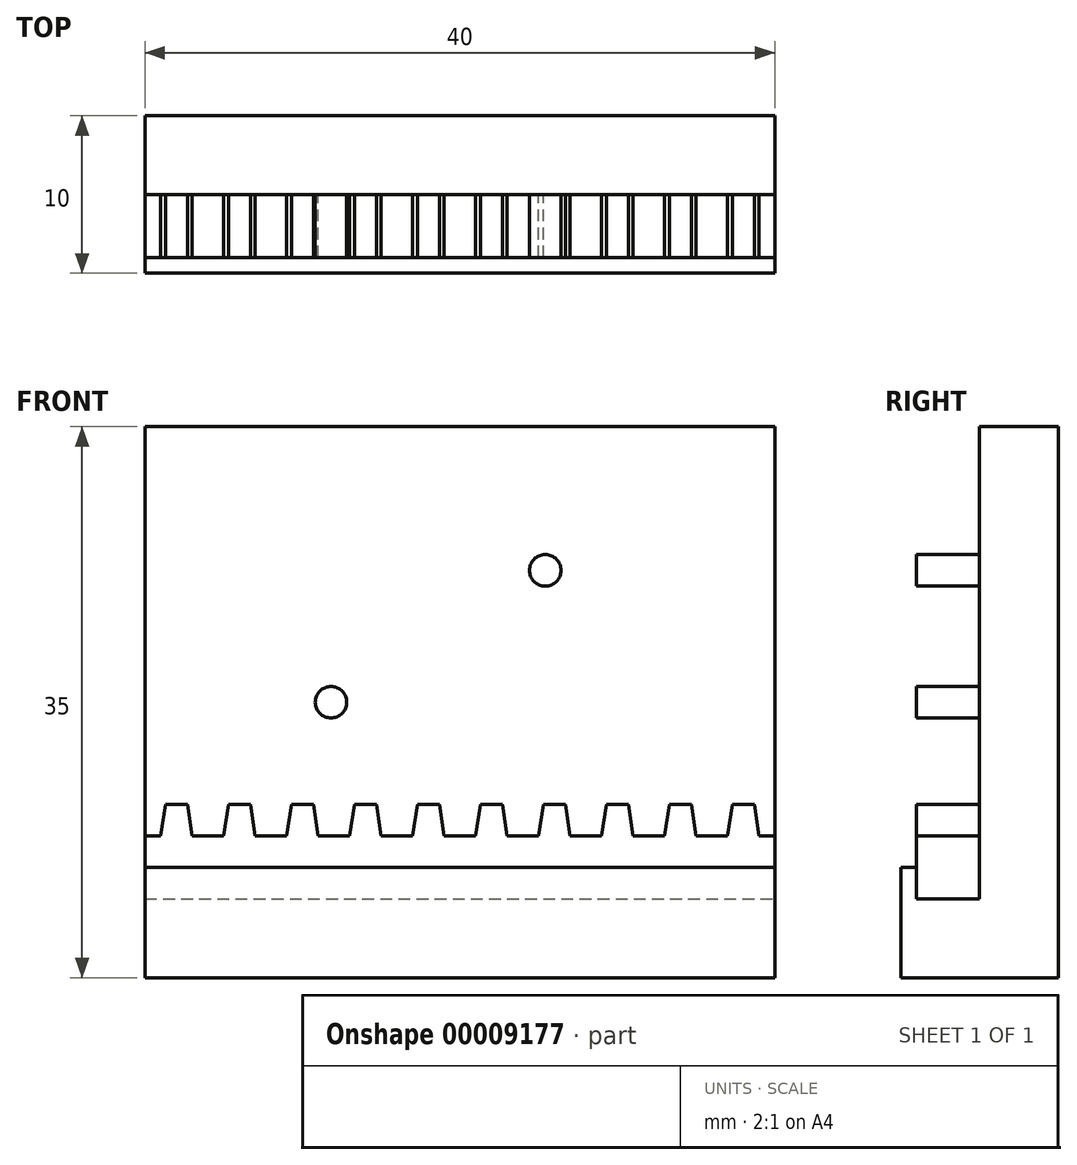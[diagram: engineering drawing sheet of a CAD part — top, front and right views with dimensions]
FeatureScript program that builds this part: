
annotation { "Feature Type Name" : "Feature", "Feature Type Description" : "" }
export const myFeature = defineFeature(function(context is Context, id is Id, definition is map)
    precondition{}
    {
        {
            var Q0;
            Q0=qCreatedBy(makeId("Front.planeOp"),FACE);
            var sketch = newSketch(context, id + "F0", { "sketchPlane" : qUnion([Q0])});
            skLineSegment(sketch, "E0.rect.bottom", {"start": v(-20, 17.5) * mm, "end": v(20, 17.5) * mm});
            skLineSegment(sketch, "E0.rect.top", {"start": v(-20, -17.5) * mm, "end": v(20, -17.5) * mm});
            skLineSegment(sketch, "E0.rect.left", {"start": v(-20, 17.5) * mm, "end": v(-20, -17.5) * mm});
            skLineSegment(sketch, "E0.rect.right", {"start": v(20, 17.5) * mm, "end": v(20, -17.5) * mm});
            skPoint(sketch, "E0.rect.middle", {"position": v(0, 0) * mm});
            skSolve(sketch);
        }
        {
            var Q0;
            Q0 = qSketchRegion(id + "F0", true);
            extrude(context, id + "F1", {"entities" : qUnion([Q0]), "depth" : 10 * mm});
        }
        {
            var Q0;
            Q0=makeQuery(id+"F1.opExtrude","CAP_FACE",FACE,{"disambiguationData":[OSD([sQuery(id+"F0.wireOp",EDGE,"E0.rect.bottom"),sQuery(id+"F0.wireOp",EDGE,"E0.rect.top"),sQuery(id+"F0.wireOp",EDGE,"E0.rect.left"),sQuery(id+"F0.wireOp",EDGE,"E0.rect.right")])],"isStart":false});
            var sketch = newSketch(context, id + "F2", { "sketchPlane" : qUnion([Q0])});
            skLineSegment(sketch, "E1.bottom", {"start": v(-20, 17.5) * mm, "end": v(20, 17.5) * mm});
            skLineSegment(sketch, "E1.top", {"start": v(-20, -12.5) * mm, "end": v(20, -12.5) * mm});
            skLineSegment(sketch, "E1.left", {"start": v(-20, 17.5) * mm, "end": v(-20, -12.5) * mm});
            skLineSegment(sketch, "E1.right", {"start": v(20, 17.5) * mm, "end": v(20, -12.5) * mm});
            skSolve(sketch);
        }
        {
            var Q0;
            Q0=makeQuery(id+"F2.imprint","IMPRINT",FACE,{"disambiguationData":[TD([[makeQuery(id+"F2.imprint","IMPRINT",EDGE,{"derivedFrom":sQuery(id+"F2.wireOp",EDGE,"E1.bottom")}),-1.0]])]});
            extrude(context, id + "F3", {"entities" : qUnion([Q0]), "operationType" : NewBodyOperationType.REMOVE, "oppositeDirection" : true, "depth" : 5 * mm});
        }
        {
            var Q0;
            Q0=makeQuery(id+"F1.opExtrude","SWEPT_FACE",FACE,{"disambiguationData":[OSD([sQuery(id+"F0.wireOp",EDGE,"E0.rect.right")])]});
            var sketch = newSketch(context, id + "F4", { "sketchPlane" : qUnion([Q0])});
            skLineSegment(sketch, "E2.bottom", {"start": v(-10, -12.5) * mm, "end": v(-9, -12.5) * mm});
            skLineSegment(sketch, "E2.top", {"start": v(-10, -10.5) * mm, "end": v(-9, -10.5) * mm});
            skLineSegment(sketch, "E2.left", {"start": v(-10, -12.5) * mm, "end": v(-10, -10.5) * mm});
            skLineSegment(sketch, "E2.right", {"start": v(-9, -12.5) * mm, "end": v(-9, -10.5) * mm});
            skSolve(sketch);
        }
        {
            var Q0;
            Q0 = qSketchRegion(id + "F4", true);
            var Q1;
            Q1=makeQuery(id+"F1.opExtrude","SWEPT_FACE",FACE,{"disambiguationData":[OSD([sQuery(id+"F0.wireOp",EDGE,"E0.rect.left")])]});
            extrude(context, id + "F5", {"entities" : qUnion([Q0]), "operationType" : NewBodyOperationType.ADD, "endBound" : BoundingType.UP_TO_SURFACE, "oppositeDirection" : true, "endBoundEntityFace" : qUnion([Q1]), "depth" : 25 * mm});
        }
        {
            var Q0;
            Q0=makeQuery(id+"F3.boolean.opBoolean","COPY",FACE,{"derivedFrom":makeQuery(id+"F3.opExtrude","CAP_FACE",FACE,{"disambiguationData":[OSD([sQuery(id+"F2.wireOp",EDGE,"E1.bottom"),sQuery(id+"F2.wireOp",EDGE,"E1.top"),sQuery(id+"F2.wireOp",EDGE,"E1.left"),sQuery(id+"F2.wireOp",EDGE,"E1.right")])],"isStart":false})});
            var sketch = newSketch(context, id + "F6", { "sketchPlane" : qUnion([Q0])});
            skCircle(sketch, "E3", {"center": v(-8.18, 0) * mm, "radius": 1 * mm});
            skCircle(sketch, "E4", {"center": v(5.42, 8.37) * mm, "radius": 1 * mm});
            skSolve(sketch);
        }
        {
            var Q0;
            Q0 = qSketchRegion(id + "F6", true);
            extrude(context, id + "F7", {"entities" : qUnion([Q0]), "operationType" : NewBodyOperationType.ADD, "depth" : 4 * mm});
        }
        {
            var Q0;
            Q0=makeQuery(id+"F3.boolean.opBoolean","COPY",FACE,{"derivedFrom":makeQuery(id+"F3.opExtrude","CAP_FACE",FACE,{"disambiguationData":[OSD([sQuery(id+"F2.wireOp",EDGE,"E1.bottom"),sQuery(id+"F2.wireOp",EDGE,"E1.top"),sQuery(id+"F2.wireOp",EDGE,"E1.left"),sQuery(id+"F2.wireOp",EDGE,"E1.right")])],"isStart":false})});
            var sketch = newSketch(context, id + "F8", { "sketchPlane" : qUnion([Q0])});
            skLineSegment(sketch, "E5.bottom", {"start": v(-20, -12.5) * mm, "end": v(20, -12.5) * mm});
            skLineSegment(sketch, "E5.top", {"start": v(-20, -8.5) * mm, "end": v(20, -8.5) * mm});
            skLineSegment(sketch, "E5.left", {"start": v(-20, -12.5) * mm, "end": v(-20, -8.5) * mm});
            skLineSegment(sketch, "E5.right", {"start": v(20, -12.5) * mm, "end": v(20, -8.5) * mm});
            skLineSegment(sketch, "E6", {"start": v(-18, -8.5) * mm, "end": v(-18, -12.5) * mm, "construction": true});
            skLineSegment(sketch, "E7", {"start": v(-19, -8.5) * mm, "end": v(-18.7, -6.5) * mm});
            skLineSegment(sketch, "E8", {"start": v(-18.7, -6.5) * mm, "end": v(-18, -6.5) * mm});
            skLineSegment(sketch, "E9.MirrorCS", {"start": v(-17, -8.5) * mm, "end": v(-17.3, -6.5) * mm});
            skLineSegment(sketch, "E10.MirrorCS", {"start": v(-17.3, -6.5) * mm, "end": v(-18, -6.5) * mm});
            skLineSegment(sketch, "E11.1.0.0", {"start": v(-15, -8.5) * mm, "end": v(-14.7, -6.5) * mm});
            skLineSegment(sketch, "E11.1.0.1", {"start": v(-14.7, -6.5) * mm, "end": v(-14, -6.5) * mm});
            skLineSegment(sketch, "E11.1.0.2", {"start": v(-13.3, -6.5) * mm, "end": v(-14, -6.5) * mm});
            skLineSegment(sketch, "E11.1.0.3", {"start": v(-13, -8.5) * mm, "end": v(-13.3, -6.5) * mm});
            skLineSegment(sketch, "E11.2.0.0", {"start": v(-11, -8.5) * mm, "end": v(-10.7, -6.5) * mm});
            skLineSegment(sketch, "E11.2.0.1", {"start": v(-10.7, -6.5) * mm, "end": v(-10, -6.5) * mm});
            skLineSegment(sketch, "E11.2.0.2", {"start": v(-9.3, -6.5) * mm, "end": v(-10, -6.5) * mm});
            skLineSegment(sketch, "E11.2.0.3", {"start": v(-9, -8.5) * mm, "end": v(-9.3, -6.5) * mm});
            skLineSegment(sketch, "E11.3.0.0", {"start": v(-7, -8.5) * mm, "end": v(-6.7, -6.5) * mm});
            skLineSegment(sketch, "E11.3.0.1", {"start": v(-6.7, -6.5) * mm, "end": v(-6, -6.5) * mm});
            skLineSegment(sketch, "E11.3.0.2", {"start": v(-5.3, -6.5) * mm, "end": v(-6, -6.5) * mm});
            skLineSegment(sketch, "E11.3.0.3", {"start": v(-5, -8.5) * mm, "end": v(-5.3, -6.5) * mm});
            skLineSegment(sketch, "E11.4.0.0", {"start": v(-3, -8.5) * mm, "end": v(-2.7, -6.5) * mm});
            skLineSegment(sketch, "E11.4.0.1", {"start": v(-2.7, -6.5) * mm, "end": v(-2, -6.5) * mm});
            skLineSegment(sketch, "E11.4.0.2", {"start": v(-1.3, -6.5) * mm, "end": v(-2, -6.5) * mm});
            skLineSegment(sketch, "E11.4.0.3", {"start": v(-1, -8.5) * mm, "end": v(-1.3, -6.5) * mm});
            skLineSegment(sketch, "E11.5.0.0", {"start": v(1, -8.5) * mm, "end": v(1.3, -6.5) * mm});
            skLineSegment(sketch, "E11.5.0.1", {"start": v(1.3, -6.5) * mm, "end": v(2, -6.5) * mm});
            skLineSegment(sketch, "E11.5.0.2", {"start": v(2.7, -6.5) * mm, "end": v(2, -6.5) * mm});
            skLineSegment(sketch, "E11.5.0.3", {"start": v(3, -8.5) * mm, "end": v(2.7, -6.5) * mm});
            skLineSegment(sketch, "E11.6.0.0", {"start": v(5, -8.5) * mm, "end": v(5.3, -6.5) * mm});
            skLineSegment(sketch, "E11.6.0.1", {"start": v(5.3, -6.5) * mm, "end": v(6, -6.5) * mm});
            skLineSegment(sketch, "E11.6.0.2", {"start": v(6.7, -6.5) * mm, "end": v(6, -6.5) * mm});
            skLineSegment(sketch, "E11.6.0.3", {"start": v(7, -8.5) * mm, "end": v(6.7, -6.5) * mm});
            skLineSegment(sketch, "E11.7.0.0", {"start": v(9, -8.5) * mm, "end": v(9.3, -6.5) * mm});
            skLineSegment(sketch, "E11.7.0.1", {"start": v(9.3, -6.5) * mm, "end": v(10, -6.5) * mm});
            skLineSegment(sketch, "E11.7.0.2", {"start": v(10.7, -6.5) * mm, "end": v(10, -6.5) * mm});
            skLineSegment(sketch, "E11.7.0.3", {"start": v(11, -8.5) * mm, "end": v(10.7, -6.5) * mm});
            skLineSegment(sketch, "E11.8.0.0", {"start": v(13, -8.5) * mm, "end": v(13.3, -6.5) * mm});
            skLineSegment(sketch, "E11.8.0.1", {"start": v(13.3, -6.5) * mm, "end": v(14, -6.5) * mm});
            skLineSegment(sketch, "E11.8.0.2", {"start": v(14.7, -6.5) * mm, "end": v(14, -6.5) * mm});
            skLineSegment(sketch, "E11.8.0.3", {"start": v(15, -8.5) * mm, "end": v(14.7, -6.5) * mm});
            skLineSegment(sketch, "E11.9.0.0", {"start": v(17, -8.5) * mm, "end": v(17.3, -6.5) * mm});
            skLineSegment(sketch, "E11.9.0.1", {"start": v(17.3, -6.5) * mm, "end": v(18, -6.5) * mm});
            skLineSegment(sketch, "E11.9.0.2", {"start": v(18.7, -6.5) * mm, "end": v(18, -6.5) * mm});
            skLineSegment(sketch, "E11.9.0.3", {"start": v(19, -8.5) * mm, "end": v(18.7, -6.5) * mm});
            skLineSegment(sketch, "E11.direction1", {"start": v(-19, -8.5) * mm, "end": v(-15, -8.5) * mm, "construction": true});
            skSolve(sketch);
        }
        {
            var Q0;
            Q0 = qSketchRegion(id + "F8", true);
            extrude(context, id + "F9", {"entities" : qUnion([Q0]), "depth" : 4 * mm});
        }
    });
